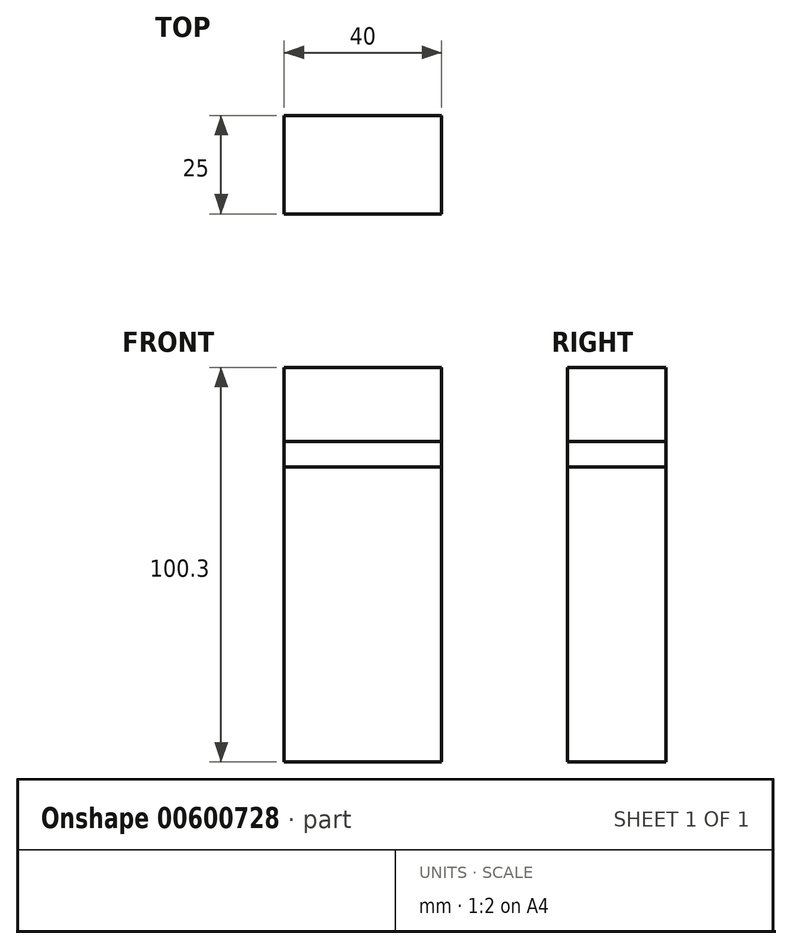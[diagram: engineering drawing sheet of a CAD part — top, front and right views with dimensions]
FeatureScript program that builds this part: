
annotation { "Feature Type Name" : "Feature", "Feature Type Description" : "" }
export const myFeature = defineFeature(function(context is Context, id is Id, definition is map)
    precondition{}
    {
        {
            var Q0;
            Q0=qCreatedBy(makeId("Front.planeOp"),FACE);
            var sketch = newSketch(context, id + "F0", { "sketchPlane" : qUnion([Q0])});
            skLineSegment(sketch, "E0", {"start": v(0, 0) * mm, "end": v(0, -20) * mm, "construction": true});
            skLineSegment(sketch, "E1", {"start": v(0, -20) * mm, "end": v(-20, -20) * mm});
            skLineSegment(sketch, "E2", {"start": v(-20, -20) * mm, "end": v(-20, 55) * mm});
            skLineSegment(sketch, "E3", {"start": v(-20, 55) * mm, "end": v(-20, 61.47) * mm});
            skPoint(sketch, "E3.endSnap0", {"position": v(-20, 17.5) * mm});
            skLineSegment(sketch, "E4", {"start": v(-20, 61.47) * mm, "end": v(-20, 80.3) * mm});
            skLineSegment(sketch, "E5", {"start": v(-20, 80.3) * mm, "end": v(20, 80.3) * mm});
            skLineSegment(sketch, "E6", {"start": v(20, 80.3) * mm, "end": v(20, -20) * mm});
            skLineSegment(sketch, "E7", {"start": v(20, -20) * mm, "end": v(0, -20) * mm});
            skLineSegment(sketch, "E8", {"start": v(-20, 61.47) * mm, "end": v(20, 61.47) * mm});
            skLineSegment(sketch, "E9", {"start": v(-20, 55) * mm, "end": v(20, 55) * mm});
            skSolve(sketch);
        }
        {
            var Q0;
            Q0=makeQuery(id+"F0.imprint","IMPRINT",FACE,{"disambiguationData":[TD([[makeQuery(id+"F0.imprint","IMPRINT",EDGE,{"derivedFrom":sQuery(id+"F0.wireOp",EDGE,"E4")}),-1.0]])]});
            extrude(context, id + "F1", {"entities" : qUnion([Q0]), "depth" : 25 * mm, "offsetDistance" : 25 * mm});
        }
        {
            var Q0;
            Q0=makeQuery(id+"F0.imprint","IMPRINT",FACE,{"disambiguationData":[TD([[makeQuery(id+"F0.imprint","IMPRINT",EDGE,{"derivedFrom":sQuery(id+"F0.wireOp",EDGE,"E3")}),-1.0]])]});
            extrude(context, id + "F2", {"entities" : qUnion([Q0]), "depth" : 25 * mm, "offsetDistance" : 25 * mm});
        }
        {
            var Q0;
            Q0=makeQuery(id+"F0.imprint","IMPRINT",FACE,{"disambiguationData":[TD([[makeQuery(id+"F0.imprint","IMPRINT",EDGE,{"derivedFrom":sQuery(id+"F0.wireOp",EDGE,"E1")}),-1.0]])]});
            extrude(context, id + "F3", {"entities" : qUnion([Q0]), "depth" : 25 * mm, "offsetDistance" : 25 * mm});
        }
    });
